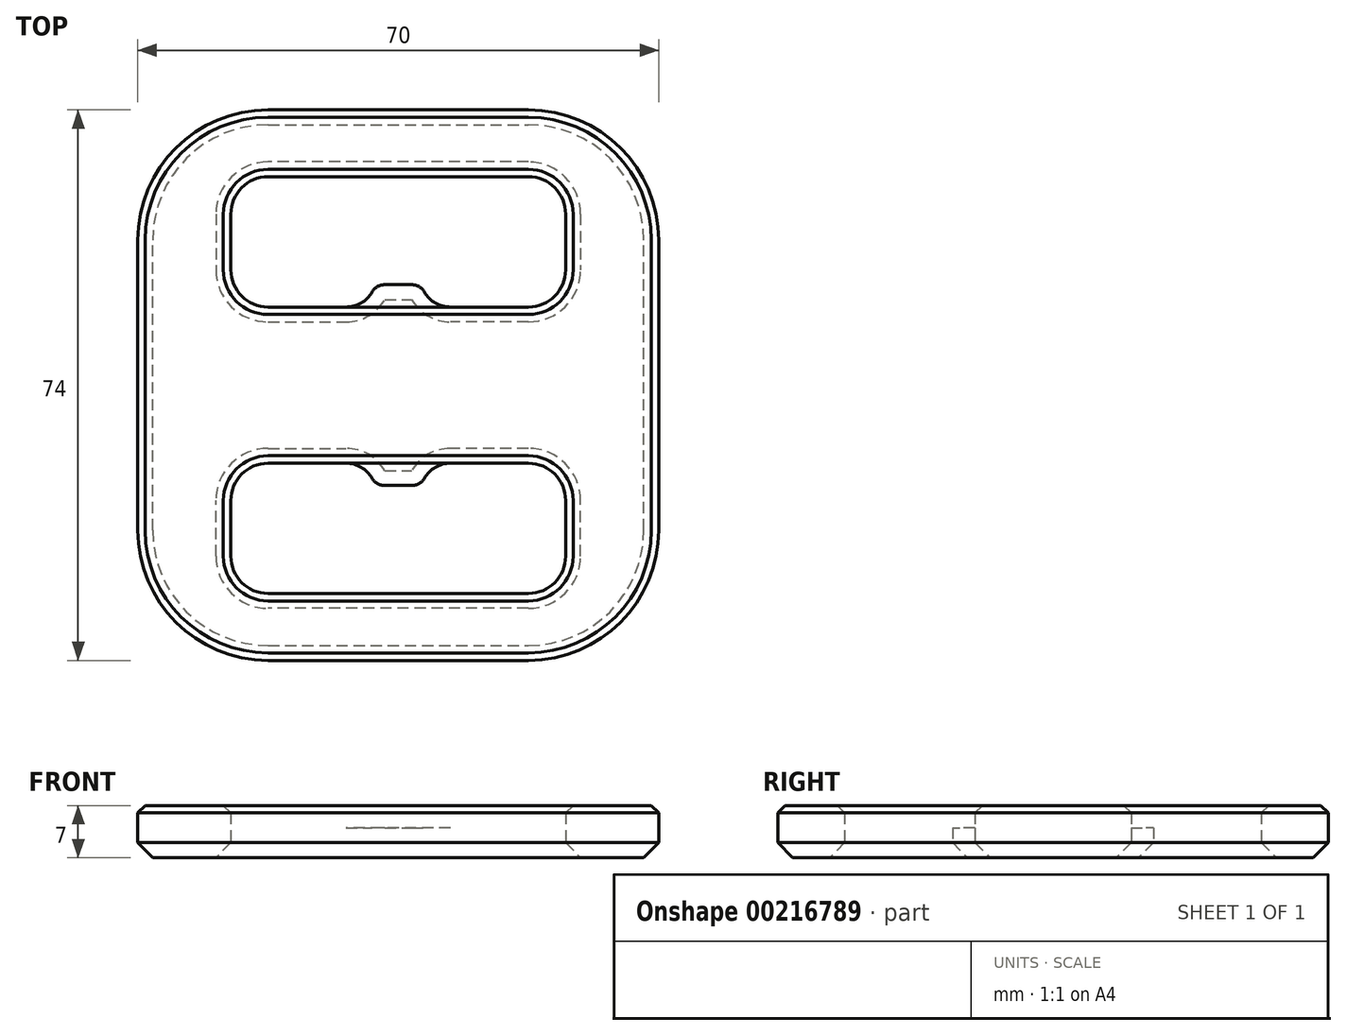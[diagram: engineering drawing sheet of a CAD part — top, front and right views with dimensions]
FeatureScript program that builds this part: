
annotation { "Feature Type Name" : "Feature", "Feature Type Description" : "" }
export const myFeature = defineFeature(function(context is Context, id is Id, definition is map)
    precondition{}
    {
        {
            var Q0;
            Q0=qCreatedBy(makeId("Top.planeOp"),FACE);
            var sketch = newSketch(context, id + "F0", { "sketchPlane" : qUnion([Q0])});
            skLineSegment(sketch, "E0", {"start": v(-17.5, 10.5) * mm, "end": v(0, 10.5) * mm});
            skLineSegment(sketch, "E1", {"start": v(-22.5, 15.5) * mm, "end": v(-22.5, 23) * mm});
            skLineSegment(sketch, "E2", {"start": v(-17.5, 28) * mm, "end": v(0, 28) * mm});
            skLineSegment(sketch, "E3.bottom", {"start": v(-17.5, 37) * mm, "end": v(0, 37) * mm});
            skLineSegment(sketch, "E3.top", {"start": v(-35, 0) * mm, "end": v(0, 0) * mm});
            skLineSegment(sketch, "E3.left", {"start": v(-35, 19.5) * mm, "end": v(-35, 0) * mm});
            skPoint(sketch, "E4.visualSharp", {"position": v(-22.5, 10.5) * mm});
            skArc(sketch, "E4.filletArc", {"start": v(-22.5, 15.5) * mm, "mid": v(-21.04, 11.96) * mm, "end": v(-17.5, 10.5) * mm});
            skPoint(sketch, "E5.visualSharp", {"position": v(-22.5, 28) * mm});
            skArc(sketch, "E5.filletArc", {"start": v(-17.5, 28) * mm, "mid": v(-21.04, 26.54) * mm, "end": v(-22.5, 23) * mm});
            skPoint(sketch, "E6.visualSharp", {"position": v(-35, 37) * mm});
            skArc(sketch, "E6.filletArc", {"start": v(-17.5, 37) * mm, "mid": v(-29.87, 31.87) * mm, "end": v(-35, 19.5) * mm});
            skLineSegment(sketch, "E7", {"start": v(0, 0) * mm, "end": v(0, 10.5) * mm});
            skLineSegment(sketch, "E8.trimOffspring", {"start": v(0, 28) * mm, "end": v(0, 37) * mm});
            skSolve(sketch);
        }
        {
            var Q0;
            Q0 = qSketchRegion(id + "F0", true);
            extrude(context, id + "F1", {"entities" : qUnion([Q0]), "depth" : 7 * mm});
        }
        {
            var Q0;
            Q0=qCreatedBy(makeId("Top.planeOp"),FACE);
            var sketch = newSketch(context, id + "F2", { "sketchPlane" : qUnion([Q0])});
            skLineSegment(sketch, "E9", {"start": v(0, 10.5) * mm, "end": v(-7, 10.5) * mm});
            skArc(sketch, "E10", {"start": v(-7, 10.5) * mm, "mid": v(-5, 11.04) * mm, "end": v(-3.54, 12.5) * mm});
            skArc(sketch, "E11", {"start": v(-1.8, 13.5) * mm, "mid": v(-2.8, 13.23) * mm, "end": v(-3.54, 12.5) * mm});
            skLineSegment(sketch, "E12", {"start": v(-1.8, 13.5) * mm, "end": v(0, 13.5) * mm});
            skPoint(sketch, "E13.orphan", {"position": v(7, 10.5) * mm});
            skLineSegment(sketch, "E14", {"start": v(0, 10.5) * mm, "end": v(0, 13.5) * mm});
            skSolve(sketch);
        }
        {
            var Q0;
            Q0=makeQuery(id+"F2.imprint","IMPRINT",FACE,{"disambiguationData":[TD([[makeQuery(id+"F2.imprint","IMPRINT",EDGE,{"derivedFrom":sQuery(id+"F2.wireOp",EDGE,"E9")}),-1.0]])]});
            extrude(context, id + "F3", {"entities" : qUnion([Q0]), "operationType" : NewBodyOperationType.ADD, "depth" : 4 * mm});
        }
        {
            var Q0;
            Q0=makeQuery(id+"F3.opExtrude","CAP_EDGE",EDGE,{"disambiguationData":[OSD([sQuery(id+"F2.wireOp",EDGE,"E12")])],"isStart":true});
            var Q1;
            Q1=makeQuery(id+"F1.opExtrude","CAP_EDGE",EDGE,{"disambiguationData":[OSD([sQuery(id+"F0.wireOp",EDGE,"E3.left")])],"isStart":true});
            chamfer(context, id + "F4", {"entities" : qUnion([Q0, Q1]), "width" : 2 * mm, "tangentPropagation" : true});
        }
        {
            var Q0;
            Q0=makeQuery(id+"F1.opExtrude","CAP_FACE",FACE,{"disambiguationData":[OSD([sQuery(id+"F0.wireOp",EDGE,"E0"),sQuery(id+"F0.wireOp",EDGE,"E1"),sQuery(id+"F0.wireOp",EDGE,"E2"),sQuery(id+"F0.wireOp",EDGE,"E3.bottom"),sQuery(id+"F0.wireOp",EDGE,"E3.top"),sQuery(id+"F0.wireOp",EDGE,"E3.left"),sQuery(id+"F0.wireOp",EDGE,"E4.filletArc"),sQuery(id+"F0.wireOp",EDGE,"E5.filletArc"),sQuery(id+"F0.wireOp",EDGE,"E6.filletArc"),sQuery(id+"F0.wireOp",EDGE,"E7"),sQuery(id+"F0.wireOp",EDGE,"E8.trimOffspring")])],"isStart":false});
            var sketch = newSketch(context, id + "F5", { "sketchPlane" : qUnion([Q0])});
            skCircle(sketch, "E15", {"center": v(0, 0) * mm, "radius": 2.38 * mm});
            skCircle(sketch, "E16", {"center": v(-3.46, 6) * mm, "radius": 2.38 * mm});
            skLineSegment(sketch, "E17", {"start": v(-3.46, 6) * mm, "end": v(0, 0) * mm, "construction": true});
            skCircle(sketch, "E18.1.0.0", {"center": v(-10.74, 6) * mm, "radius": 2.38 * mm});
            skCircle(sketch, "E18.1.0.1", {"center": v(-7.27, 0) * mm, "radius": 2.38 * mm});
            skCircle(sketch, "E18.2.0.0", {"center": v(-18.01, 6) * mm, "radius": 2.38 * mm});
            skCircle(sketch, "E18.2.0.1", {"center": v(-14.55, 0) * mm, "radius": 2.38 * mm});
            skCircle(sketch, "E18.3.0.0", {"center": v(-25.29, 6) * mm, "radius": 2.38 * mm});
            skCircle(sketch, "E18.3.0.1", {"center": v(-21.82, 0) * mm, "radius": 2.38 * mm});
            skCircle(sketch, "E18.4.0.1", {"center": v(-29.1, 0) * mm, "radius": 2.38 * mm});
            skLineSegment(sketch, "E18.direction1", {"start": v(-3.46, 6) * mm, "end": v(-10.74, 6) * mm, "construction": true});
            skCircle(sketch, "E19", {"center": v(-28.75, 12) * mm, "radius": 2.38 * mm});
            skCircle(sketch, "E20", {"center": v(-28.75, 19.34) * mm, "radius": 2.38 * mm});
            skCircle(sketch, "E21", {"center": v(0, 32.5) * mm, "radius": 2.38 * mm});
            skCircle(sketch, "E22", {"center": v(-7.34, 32.5) * mm, "radius": 2.38 * mm});
            skCircle(sketch, "E23", {"center": v(-14.68, 32.5) * mm, "radius": 2.38 * mm});
            skCircle(sketch, "E24", {"center": v(-21.96, 31.56) * mm, "radius": 2.38 * mm});
            skCircle(sketch, "E25", {"center": v(-27.31, 26.54) * mm, "radius": 2.38 * mm});
            skLineSegment(sketch, "E26", {"start": v(0, 32.5) * mm, "end": v(-7.34, 32.5) * mm, "construction": true});
            skLineSegment(sketch, "E27", {"start": v(-14.68, 32.5) * mm, "end": v(-7.34, 32.5) * mm, "construction": true});
            skLineSegment(sketch, "E28", {"start": v(-14.68, 32.5) * mm, "end": v(-21.96, 31.56) * mm, "construction": true});
            skLineSegment(sketch, "E29", {"start": v(-21.96, 31.56) * mm, "end": v(-27.31, 26.54) * mm, "construction": true});
            skLineSegment(sketch, "E30", {"start": v(-27.31, 26.54) * mm, "end": v(-28.75, 19.34) * mm, "construction": true});
            skLineSegment(sketch, "E31", {"start": v(-28.75, 12) * mm, "end": v(-28.75, 19.34) * mm, "construction": true});
            skCircle(sketch, "E32", {"center": v(-21.96, 31.56) * mm, "radius": 4.65 * mm, "construction": true});
            skCircle(sketch, "E33", {"center": v(-27.31, 26.54) * mm, "radius": 5.43 * mm, "construction": true});
            skCircle(sketch, "E34", {"center": v(-28.75, 19.34) * mm, "radius": 6.25 * mm, "construction": true});
            skLineSegment(sketch, "E35", {"start": v(-21.82, 0) * mm, "end": v(-28.75, 12) * mm, "construction": true});
            skSolve(sketch);
        }
        {
            var Q0;
            Q0=makeQuery(id+"F1.opExtrude","SWEPT_BODY",BODY,{"disambiguationData":[OSD([sQuery(id+"F0.wireOp",EDGE,"E0"),sQuery(id+"F0.wireOp",EDGE,"E1"),sQuery(id+"F0.wireOp",EDGE,"E2"),sQuery(id+"F0.wireOp",EDGE,"E3.bottom"),sQuery(id+"F0.wireOp",EDGE,"E3.top"),sQuery(id+"F0.wireOp",EDGE,"E3.left"),sQuery(id+"F0.wireOp",EDGE,"E4.filletArc"),sQuery(id+"F0.wireOp",EDGE,"E5.filletArc"),sQuery(id+"F0.wireOp",EDGE,"E6.filletArc"),sQuery(id+"F0.wireOp",EDGE,"E7"),sQuery(id+"F0.wireOp",EDGE,"E8.trimOffspring")])]});
            var Q1;
            Q1=makeQuery(id+"F3.boolean.opBoolean","MERGE",FACE,{"derivedFrom":[makeQuery(id+"F1.opExtrude","SWEPT_FACE",FACE,{"disambiguationData":[OSD([sQuery(id+"F0.wireOp",EDGE,"E7")])]}),makeQuery(id+"F3.opExtrude","SWEPT_FACE",FACE,{"disambiguationData":[OSD([sQuery(id+"F2.wireOp",EDGE,"E14")])]})]});
            mirror(context, id + "F6", {"operationType" : NewBodyOperationType.ADD, "entities" : qUnion([Q0]), "mirrorPlane" : qUnion([Q1])});
        }
        {
            var Q0;
            Q0=makeQuery(id+"F1.opExtrude","SWEPT_BODY",BODY,{"disambiguationData":[OSD([sQuery(id+"F0.wireOp",EDGE,"E0"),sQuery(id+"F0.wireOp",EDGE,"E1"),sQuery(id+"F0.wireOp",EDGE,"E2"),sQuery(id+"F0.wireOp",EDGE,"0ICMdfcP-Euht-g43s-NUM6-Az8zXy5HgtwN"),sQuery(id+"F0.wireOp",EDGE,"E3.bottom"),sQuery(id+"F0.wireOp",EDGE,"E3.top"),sQuery(id+"F0.wireOp",EDGE,"E3.left"),sQuery(id+"F0.wireOp",EDGE,"E3.right"),sQuery(id+"F0.wireOp",EDGE,"E4.filletArc"),sQuery(id+"F0.wireOp",EDGE,"2db8fde6-ad73-4574-9cbc-f3337f5bc9ee.filletArc"),sQuery(id+"F0.wireOp",EDGE,"7e460184-dd95-46a4-a0e1-e2db5f587754.filletArc"),sQuery(id+"F0.wireOp",EDGE,"E5.filletArc"),sQuery(id+"F0.wireOp",EDGE,"E6.filletArc"),sQuery(id+"F0.wireOp",EDGE,"b14bd278-06a6-4b62-9ff5-1f2ab01935d8.filletArc")])]});
            var Q1;
            Q1=makeQuery(id+"F1.opExtrude","SWEPT_FACE",FACE,{"disambiguationData":[OSD([sQuery(id+"F0.wireOp",EDGE,"E3.top")])]});
            mirror(context, id + "F7", {"operationType" : NewBodyOperationType.ADD, "entities" : qUnion([Q0]), "mirrorPlane" : qUnion([Q1])});
        }
        {
            var Q0;
            {var subQ0=makeQuery(id+"F1.opExtrude","CAP_FACE",FACE,{"disambiguationData":[OSD([sQuery(id+"F0.wireOp",EDGE,"E0"),sQuery(id+"F0.wireOp",EDGE,"E1"),sQuery(id+"F0.wireOp",EDGE,"E2"),sQuery(id+"F0.wireOp",EDGE,"E3.bottom"),sQuery(id+"F0.wireOp",EDGE,"E3.top"),sQuery(id+"F0.wireOp",EDGE,"E3.left"),sQuery(id+"F0.wireOp",EDGE,"E4.filletArc"),sQuery(id+"F0.wireOp",EDGE,"E5.filletArc"),sQuery(id+"F0.wireOp",EDGE,"E6.filletArc"),sQuery(id+"F0.wireOp",EDGE,"E7"),sQuery(id+"F0.wireOp",EDGE,"E8.trimOffspring")])],"isStart":false});var subQ1=makeQuery(id+"F6.boolean.opBoolean","MERGE",FACE,{"derivedFrom":[subQ0,makeQuery(id+"F6.opPattern","COPY",FACE,{"derivedFrom":subQ0,"instanceName":"1"})]});Q0=makeQuery(id+"F7.boolean.opBoolean","MERGE",FACE,{"derivedFrom":[subQ1,makeQuery(id+"F7.opPattern","COPY",FACE,{"derivedFrom":subQ1,"instanceName":"1"})]});}
            chamfer(context, id + "F8", {"entities" : qUnion([Q0]), "width" : 1 * mm, "tangentPropagation" : true});
        }
    });
